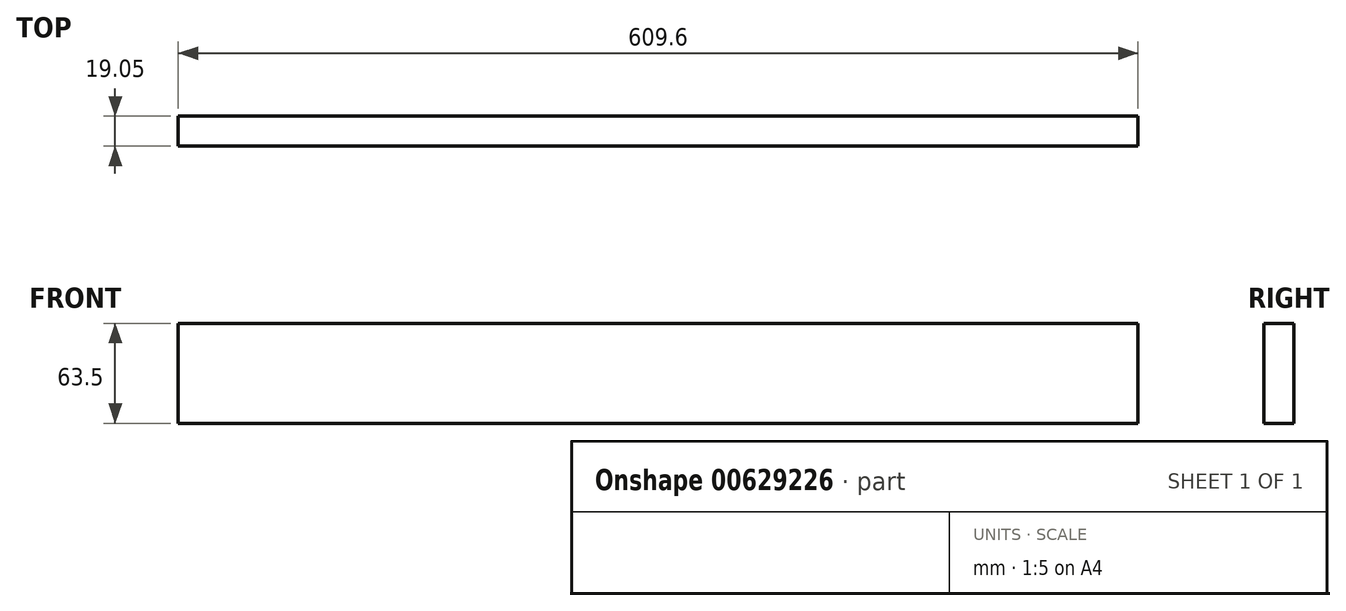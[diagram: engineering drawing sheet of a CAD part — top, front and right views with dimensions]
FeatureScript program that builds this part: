
annotation { "Feature Type Name" : "Feature", "Feature Type Description" : "" }
export const myFeature = defineFeature(function(context is Context, id is Id, definition is map)
    precondition{}
    {
        {
            var Q0;
            Q0=qCreatedBy(makeId("Front.planeOp"),FACE);
            var sketch = newSketch(context, id + "F0", { "sketchPlane" : qUnion([Q0])});
            skLineSegment(sketch, "E0.bottom", {"start": v(0, 0) * mm, "end": v(-609.6, 0) * mm});
            skLineSegment(sketch, "E0.top", {"start": v(0, 63.5) * mm, "end": v(-609.6, 63.5) * mm});
            skLineSegment(sketch, "E0.left", {"start": v(0, 0) * mm, "end": v(0, 63.5) * mm});
            skLineSegment(sketch, "E0.right", {"start": v(-609.6, 0) * mm, "end": v(-609.6, 63.5) * mm});
            skSolve(sketch);
        }
        {
            var Q0;
            Q0=makeQuery(id+"F0.imprint","IMPRINT",FACE,{"disambiguationData":[TD([[makeQuery(id+"F0.imprint","IMPRINT",EDGE,{"derivedFrom":sQuery(id+"F0.wireOp",EDGE,"E0.bottom")}),-1.0]])]});
            extrude(context, id + "F1", {"entities" : qUnion([Q0]), "oppositeDirection" : true, "depth" : 19.05 * mm, "offsetDistance" : 25.4 * mm});
        }
    });
